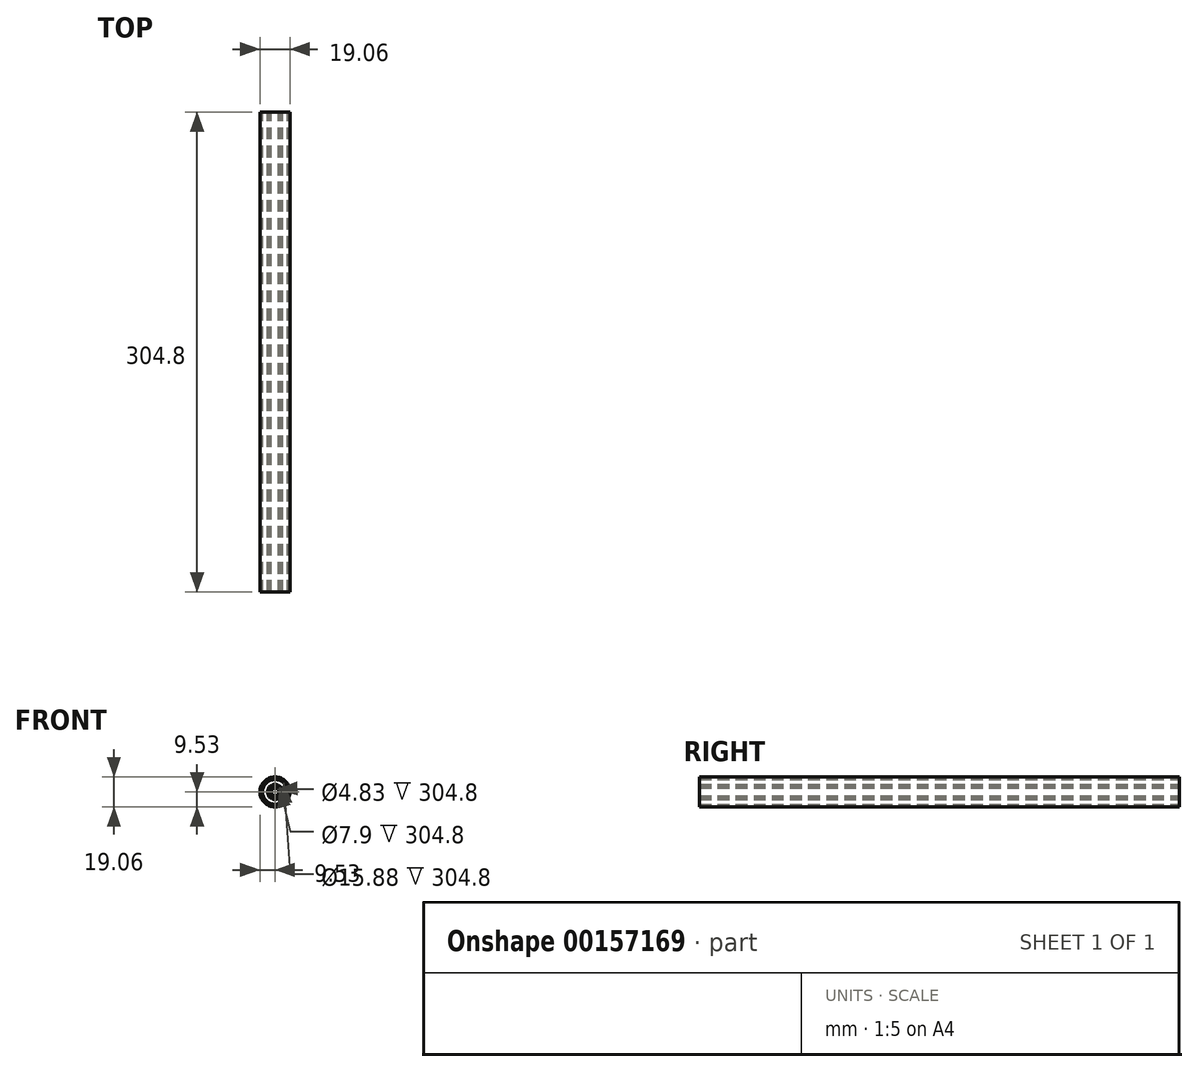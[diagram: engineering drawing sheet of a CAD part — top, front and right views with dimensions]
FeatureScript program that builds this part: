
annotation { "Feature Type Name" : "Feature", "Feature Type Description" : "" }
export const myFeature = defineFeature(function(context is Context, id is Id, definition is map)
    precondition{}
    {
        {
            var Q0;
            Q0=qCreatedBy(makeId("Front.planeOp"),FACE);
            var sketch = newSketch(context, id + "F0", { "sketchPlane" : qUnion([Q0])});
            skCircle(sketch, "E0", {"center": v(0, 0) * mm, "radius": 2.41 * mm});
            skCircle(sketch, "E1", {"center": v(0, 0) * mm, "radius": 3.18 * mm});
            skCircle(sketch, "E2", {"center": v(0, 0) * mm, "radius": 3.95 * mm});
            skCircle(sketch, "E3", {"center": v(0, 0) * mm, "radius": 4.76 * mm});
            skCircle(sketch, "E4", {"center": v(0, 0) * mm, "radius": 7.94 * mm});
            skCircle(sketch, "E5", {"center": v(0, 0) * mm, "radius": 9.53 * mm});
            skSolve(sketch);
        }
        {
            var Q0;
            Q0=makeQuery(id+"F0.imprint","IMPRINT",FACE,{"disambiguationData":[TD([[makeQuery(id+"F0.imprint","IMPRINT",EDGE,{"derivedFrom":sQuery(id+"F0.wireOp",EDGE,"E0")}),-1.0]])]});
            var Q1;
            Q1=makeQuery(id+"F0.imprint","IMPRINT",FACE,{"disambiguationData":[TD([[makeQuery(id+"F0.imprint","IMPRINT",EDGE,{"derivedFrom":sQuery(id+"F0.wireOp",EDGE,"E2")}),-1.0]])]});
            var Q2;
            Q2=makeQuery(id+"F0.imprint","IMPRINT",FACE,{"disambiguationData":[TD([[makeQuery(id+"F0.imprint","IMPRINT",EDGE,{"derivedFrom":sQuery(id+"F0.wireOp",EDGE,"E4")}),-1.0]])]});
            extrude(context, id + "F1", {"entities" : qUnion([Q0, Q1, Q2]), "depth" : 304.8 * mm});
        }
    });
